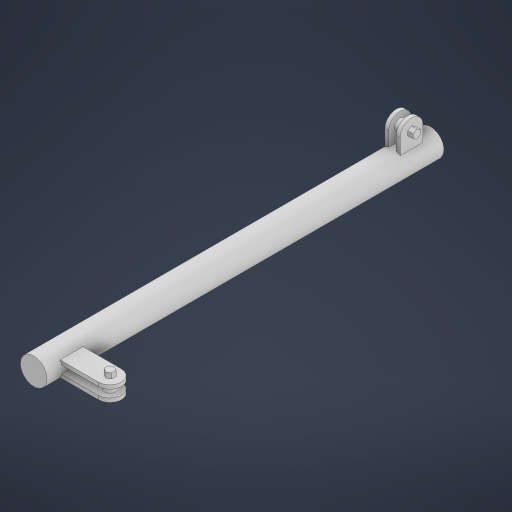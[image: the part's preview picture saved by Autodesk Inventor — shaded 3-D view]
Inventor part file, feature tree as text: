
AUTODESK INVENTOR PART (.ipt)
format: ipt  version: 2023 (Build 270158000, 158)  size: 282,112 bytes
history: native  units: in
note: dims shown in document units (in); Inventor stores cm internally (conversion verified against a paired STEP export)
features: extrude x7, sketch x7, mirror x2, fillet x1
ambient origin geometry x8: Origin, YZ Plane, XZ Plane, XY Plane, X Axis, Y Axis, Z Axis, Center Point
bodies: Solid1 (feature_tree)
feature tree (17):
  extrude  "Extrusion1"  Depth=52.0in TaperAngle=0.0deg
  extrude  "Extrusion2"  Depth=0.5in
  extrude  "Extrusion3"  Depth=2.0in
  fillet  "Fillet1"  Radius=5.0in
  extrude  "Extrusion4"  Depth=0.5in
  extrude  "Extrusion5"  Depth=3.0in
  extrude  "Extrusion6"  Depth=8.0in TaperAngle=0.0deg
  extrude  "Extrusion7"  Depth=8.0in TaperAngle=0.0deg
  mirror  "Mirror2"
  mirror  "Mirror3"
  sketch  "Sketch1"  dims[d0=3.5in d1=52.0in d2=0.0in]
  sketch  "Sketch2"  dims[d3=3.0in d4=0.5in]
  sketch  "Sketch3"  dims[d5=0.5in d6=2.0in d7=5.0in d8=0.0in]
  sketch  "Sketch4"  dims[d9=1.5in d10=0.5in]
  sketch  "Sketch5"  dims[d11=0.5in d12=3.0in]
  sketch  "Sketch6"  dims[d13=2.0in d14=8.0in d15=0.0in]
  sketch  "Sketch7"  dims[d16=1.5in d17=8.0in d18=0.0in d19=1.5in d20=1.0in d21=0.0in d22=1.0in d23=0.7in d24=0.0in d25=1.0in d26=0.7in d27=0.0in]
